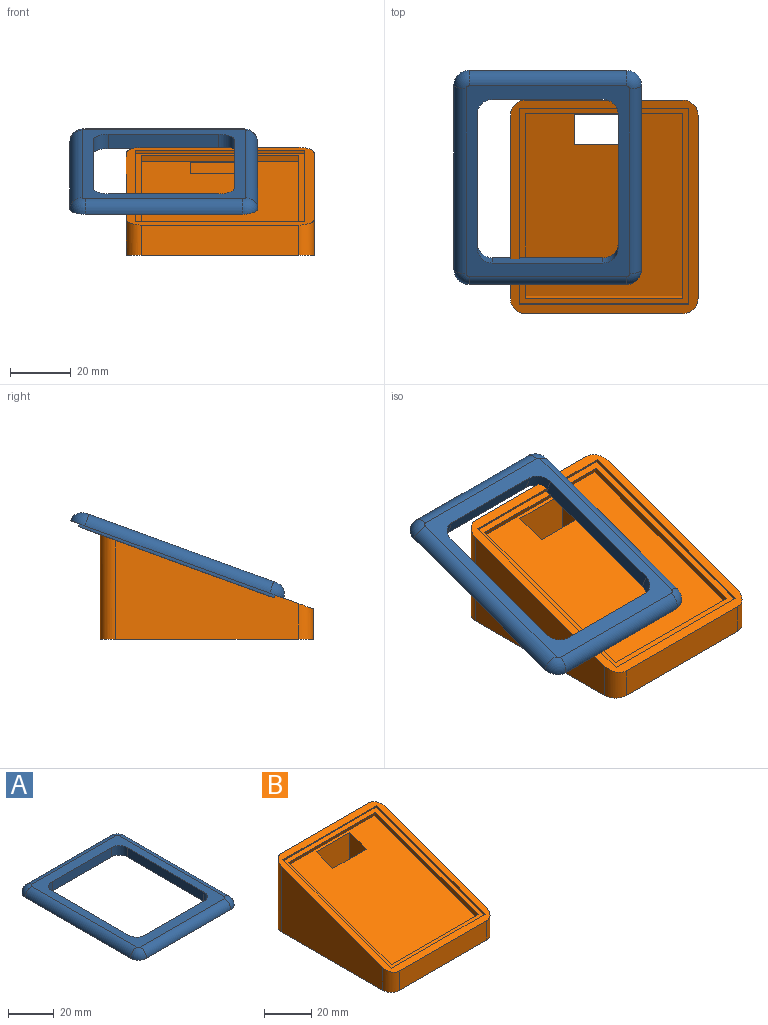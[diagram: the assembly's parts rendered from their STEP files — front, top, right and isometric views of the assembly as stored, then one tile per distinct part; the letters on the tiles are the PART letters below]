
ASSEMBLY  parts=2 mates=1
PART A: 23 faces, bbox 62x75x5 mm
  f0: plane 36.5x5mm, normal (0,-1,0), area 182.5mm2, adj f4,f6,f9,f22
  f1: plane 47.5x5mm, normal (-1,0,0), area 237.5mm2, adj f4,f6,f7,f22
  f2: plane 36.5x5mm, normal (0,1,0), area 182.5mm2, adj f4,f7,f8,f22
  f3: plane 47.5x5mm, normal (1,0,0), area 237.5mm2, adj f4,f8,f9,f22
  f4: plane 67x54mm, normal (0,0,1), area 964.9mm2, adj f0,f1,f2,f3,f6,f7,f8,f9
  f5: plane 75x62mm, normal (0,0,-1), area 764.5mm2, adj f10,f11,f12,f13,f14,f15,f16,f17
  f6: cylinder r=5mm len=5mm, axis (0,0,-1), area 39.3mm2, adj f0,f1,f4,f22
  f7: cylinder r=5mm len=5mm, axis (0,0,1), area 39.3mm2, adj f1,f2,f4,f22
  f8: cylinder r=5mm len=5mm, axis (0,0,-1), area 39.3mm2, adj f2,f3,f4,f22
  f9: cylinder r=5mm len=5mm, axis (0,0,1), area 39.3mm2, adj f0,f3,f4,f22
  f10: cylinder r=4mm len=65mm, axis (0,-1,0), area 408.4mm2, adj f4,f5,f11,f12
  f11: torus R=1mm, axis (0,0,1), area 35mm2, adj f4,f5,f10,f13
  f12: torus R=1mm, axis (0,0,1), area 35mm2, adj f4,f5,f10,f14
  f13: cylinder r=4mm len=52mm, axis (1,0,0), area 326.7mm2, adj f4,f5,f11,f15
  f14: cylinder r=4mm len=52mm, axis (-1,0,0), area 326.7mm2, adj f4,f5,f12,f16
  f15: torus R=1mm, axis (0,0,1), area 35mm2, adj f4,f5,f13,f17
  f16: torus R=1mm, axis (0,0,1), area 35mm2, adj f4,f5,f14,f17
  f17: cylinder r=4mm len=65mm, axis (0,1,0), area 408.4mm2, adj f4,f5,f15,f16
  f18: plane 69x1mm, normal (-1,0,0), area 69mm2, adj f5,f19,f21,f22
  f19: plane 56x1mm, normal (0,1,0), area 56mm2, adj f5,f18,f20,f22
  f20: plane 69x1mm, normal (1,0,0), area 69mm2, adj f5,f19,f21,f22
  f21: plane 56x1mm, normal (0,-1,0), area 56mm2, adj f5,f18,f20,f22
  f22: plane 69x56mm, normal (0,0,-1), area 1211.7mm2, adj f0,f1,f2,f3,f6,f7,f8,f9
PART B: 26 faces, bbox 62x70.5x35.7 mm
  f0: plane 61.76x24.11mm, normal (-1,0,0), area 130mm2, adj f1,f3,f10,f25
  f1: plane 52x1.88mm, normal (0,-0.94,-0.34), area 104mm2, adj f0,f2,f10,f25
  f2: plane 61.76x24.11mm, normal (1,0,0), area 130mm2, adj f1,f3,f10,f25
  f3: plane 52x1.88mm, normal (0,0.94,0.34), area 104mm2, adj f0,f2,f10,f25
  f4: plane 70.48x62mm, normal (0,-0.34,0.94), area 763.2mm2, adj f5,f7,f8,f9,f15,f16,f17,f18
  f5: plane 52x10mm, normal (0,-1,0), area 520mm2, adj f4,f6,f16,f18
  f6: plane 70.48x62mm, normal (0,0,-1), area 4114.9mm2, adj f5,f7,f8,f9,f11,f12,f13,f14
  f7: plane 52x35.65mm, normal (0,1,0), area 1853.9mm2, adj f4,f6,f15,f17
  f8: plane 60.48x33.83mm, normal (1,0,0), area 1380.4mm2, adj f4,f6,f17,f18
  f9: plane 60.48x33.83mm, normal (-1,0,0), area 1380.4mm2, adj f4,f6,f15,f16
  f10: plane 61.08x52mm, normal (0,-0.34,0.94), area 3167.2mm2, adj f0,f1,f2,f3,f11,f12,f13,f14
  f11: plane 30.75x20mm, normal (0,-1,0), area 615mm2, adj f6,f10,f12,f14
  f12: plane 30.75x10mm, normal (1,0,0), area 289.3mm2, adj f6,f10,f11,f13
  f13: plane 27.11x20mm, normal (0,1,0), area 542.2mm2, adj f6,f10,f12,f14
  f14: plane 30.75x10mm, normal (-1,0,0), area 289.3mm2, adj f6,f10,f11,f13
  f15: cylinder r=5mm len=35.65mm, axis (0,0,1), area 274.8mm2, adj f4,f6,f7,f9
  f16: cylinder r=5mm len=11.82mm, axis (0,0,-1), area 83.7mm2, adj f4,f5,f6,f9
  f17: cylinder r=5mm len=35.65mm, axis (0,0,-1), area 274.8mm2, adj f4,f6,f7,f8
  f18: cylinder r=5mm len=11.82mm, axis (0,0,1), area 83.7mm2, adj f4,f5,f6,f8
  f19: cylinder r=3.25mm len=6.5mm, axis (0,0,-1), area 122.5mm2, adj f6,f20
  f20: plane 6.5x6.5mm, normal (0,0,-1), area 33.2mm2, adj f19
  f21: plane 65.18x24.54mm, normal (1,0,0), area 69mm2, adj f4,f22,f24,f25
  f22: plane 56x0.94mm, normal (0,0.94,0.34), area 56mm2, adj f4,f21,f23,f25
  f23: plane 65.18x24.54mm, normal (-1,0,0), area 69mm2, adj f4,f22,f24,f25
  f24: plane 56x0.94mm, normal (0,-0.94,-0.34), area 56mm2, adj f4,f21,f23,f25
  f25: plane 64.84x56mm, normal (0,-0.34,0.94), area 484mm2, adj f0,f1,f2,f3,f21,f22,f23,f24
PLACE A rot(axis=(1,0,0),20deg) t=(-55.18,0.19,25.74)mm
PLACE B t=(-36.5,-9.63,-0.66)mm fixed
MATE planar A.f11 <-> B.f4  axis (0,0.34,-0.94) through (-29.18,30.73,36.86)mm
